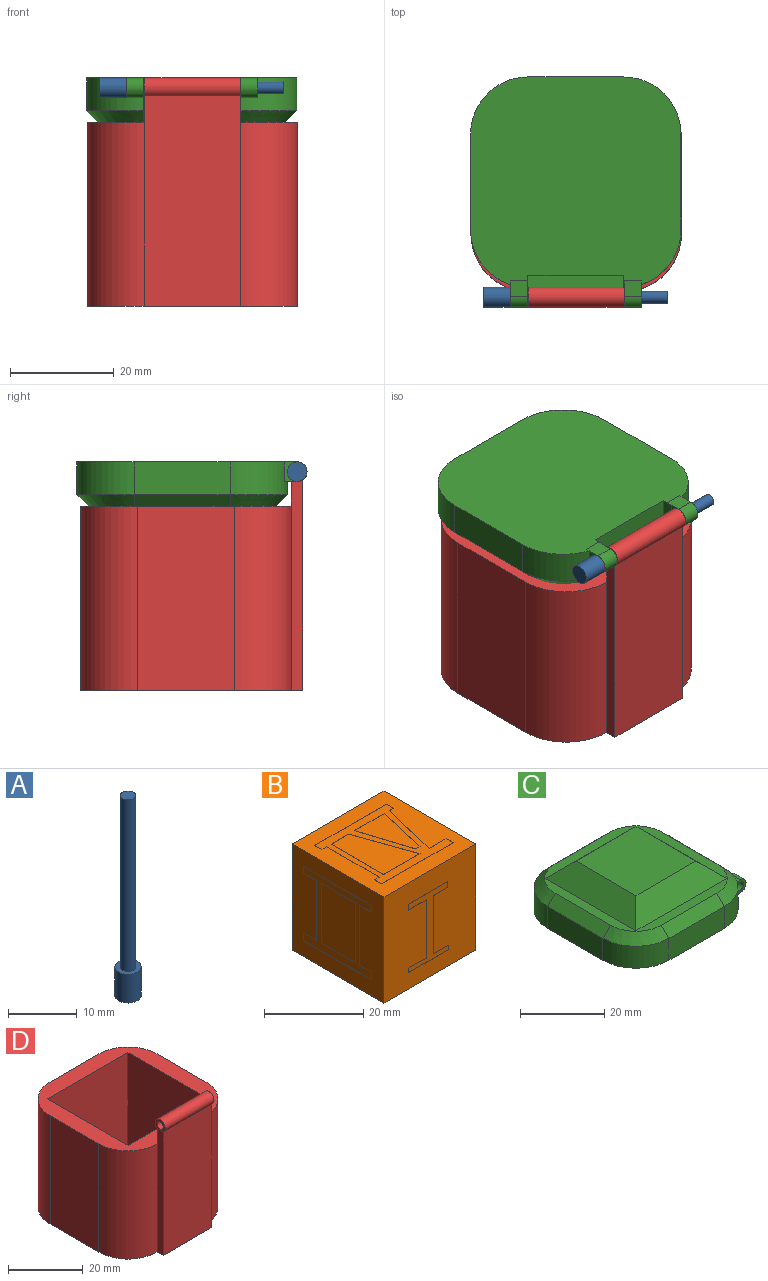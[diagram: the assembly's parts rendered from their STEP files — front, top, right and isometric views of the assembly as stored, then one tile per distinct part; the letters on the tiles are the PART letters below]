
ASSEMBLY  parts=4 mates=3
PART A: 5 faces, bbox 3.8x3.8x35.6 mm
  f0: cylinder r=1.91mm len=5.08mm, axis (0,0,-1), area 60.8mm2, adj f1,f2
  f1: plane 3.81x3.81mm, normal (0,0,1), area 7.4mm2, adj f0,f3
  f2: plane 3.81x3.81mm, normal (0,0,-1), area 11.4mm2, adj f0
  f3: cylinder r=1.13mm len=30.48mm, axis (0,0,-1), area 216.5mm2, adj f1,f4
  f4: plane 2.26x2.26mm, normal (0,0,1), area 4mm2, adj f3
PART B: 123 faces, bbox 26.2x26.2x26.2 mm
  f0: plane 26.16x26.16mm, normal (0,0,-1), area 443.9mm2, adj f1,f3,f4,f5,f106,f107,f108,f109
  f1: plane 26.16x26.16mm, normal (1,0,0), area 469.8mm2, adj f0,f2,f3,f5,f85,f86,f87,f88
  f2: plane 26.16x26.16mm, normal (0,0,1), area 361.8mm2, adj f1,f3,f4,f5,f62,f63,f64,f65
  f3: plane 26.16x26.16mm, normal (0,1,0), area 306.3mm2, adj f0,f1,f2,f4,f44,f45,f46,f47
  f4: plane 26.16x26.16mm, normal (-1,0,0), area 432mm2, adj f0,f2,f3,f5,f22,f23,f24,f25
  f5: plane 26.16x26.16mm, normal (0,-1,0), area 626mm2, adj f0,f1,f2,f4,f6,f7,f8,f9
  f6: plane 11.4x0.03mm, normal (0,0,1), area 0.3mm2, adj f5,f7,f17,f18
  f7: plane 1.1x0.03mm, normal (-1,0,0), area 0mm2, adj f5,f6,f8,f18
  f8: plane 4.28x0.03mm, normal (0,0,-1), area 0.1mm2, adj f5,f7,f9,f18
  f9: plane 14.35x0.03mm, normal (-1,0,0), area 0.4mm2, adj f5,f8,f10,f18
  f10: plane 4.1x0.03mm, normal (0,0,1), area 0.1mm2, adj f5,f9,f11,f18
  f11: plane 1.4x0.03mm, normal (-1,0,0), area 0mm2, adj f5,f10,f12,f18
  f12: plane 11.21x0.03mm, normal (0,0,-1), area 0.3mm2, adj f5,f11,f13,f18
  f13: plane 1.4x0.03mm, normal (1,0,0), area 0mm2, adj f5,f12,f14,f18
  f14: plane 5.01x0.03mm, normal (0,0,1), area 0.1mm2, adj f5,f13,f15,f18
  f15: plane 14.35x0.03mm, normal (1,0,0), area 0.4mm2, adj f5,f14,f16,f18
  f16: plane 5.01x0.03mm, normal (0,0,-1), area 0.1mm2, adj f5,f15,f17,f18
  f17: plane 1.1x0.03mm, normal (1,0,0), area 0mm2, adj f5,f6,f16,f18
  f18: plane 16.85x11.4mm, normal (0,-1,0), area 58.5mm2, adj f6,f7,f8,f9,f10,f11,f12,f13
  f19: plane 14.7x0.03mm, normal (0,1,0), area 0.4mm2, adj f20,f34,f35,f36
  f20: plane 9.66x0.03mm, normal (0,0,1), area 0.2mm2, adj f19,f21,f35,f36
  f21: plane 14.7x0.03mm, normal (0,-1,0), area 0.4mm2, adj f20,f34,f35,f36
  f22: plane 3.61x0.03mm, normal (0,0,1), area 0.1mm2, adj f4,f23,f33,f35
  f23: plane 14.7x0.03mm, normal (0,-1,0), area 0.4mm2, adj f4,f22,f24,f35
  f24: plane 3.61x0.03mm, normal (0,0,-1), area 0.1mm2, adj f4,f23,f25,f35
  f25: plane 1.97x0.03mm, normal (0,-1,0), area 0.1mm2, adj f4,f24,f26,f35
  f26: plane 19.19x0.03mm, normal (0,0,1), area 0.5mm2, adj f4,f25,f27,f35
  f27: plane 1.97x0.03mm, normal (0,1,0), area 0.1mm2, adj f4,f26,f28,f35
  f28: plane 3.2x0.03mm, normal (0,0,-1), area 0.1mm2, adj f4,f27,f29,f35
  f29: plane 14.7x0.03mm, normal (0,1,0), area 0.4mm2, adj f4,f28,f30,f35
  f30: plane 3.2x0.03mm, normal (0,0,1), area 0.1mm2, adj f4,f29,f31,f35
  f31: plane 1.7x0.03mm, normal (0,1,0), area 0mm2, adj f4,f30,f32,f35
  f32: plane 19.19x0.03mm, normal (0,0,-1), area 0.5mm2, adj f4,f31,f33,f35
  f33: plane 1.7x0.03mm, normal (0,-1,0), area 0mm2, adj f4,f22,f32,f35
  f34: plane 9.66x0.03mm, normal (0,0,-1), area 0.2mm2, adj f19,f21,f35,f36
  f35: plane 19.19x18.37mm, normal (-1,0,0), area 110.5mm2, adj f19,f20,f21,f22,f23,f24,f25,f26
  f36: plane 14.7x9.66mm, normal (-1,0,0), area 142mm2, adj f19,f20,f21,f34
  f37: plane 17.41x0.03mm, normal (1,0,0), area 0.4mm2, adj f38,f56,f57,f58
  f38: plane 10.84x0.03mm, normal (0,0,1), area 0.3mm2, adj f37,f39,f57,f58
  f39: plane 17.41x0.03mm, normal (-1,0,0), area 0.4mm2, adj f38,f40,f57,f58
  f40: plane 4.28x0.03mm, normal (0,0,-1), area 0.1mm2, adj f39,f41,f57,f58
  f41: plane 17.41x0.03mm, normal (1,0,0), area 0.4mm2, adj f40,f42,f57,f58
  f42: plane 2.29x0.03mm, normal (0,0,-1), area 0.1mm2, adj f41,f43,f57,f58
  f43: plane 17.41x0.03mm, normal (-1,0,0), area 0.4mm2, adj f42,f56,f57,f58
  f44: plane 3.21x0.03mm, normal (0,0,1), area 0.1mm2, adj f3,f45,f55,f57
  f45: plane 17.41x0.03mm, normal (-1,0,0), area 0.4mm2, adj f3,f44,f46,f57
  f46: plane 3.13x0.03mm, normal (0,0,-1), area 0.1mm2, adj f3,f45,f47,f57
  f47: plane 2.91x0.03mm, normal (-1,0,0), area 0.1mm2, adj f3,f46,f48,f57
  f48: plane 21x0.03mm, normal (0,0,1), area 0.5mm2, adj f3,f47,f49,f57
  f49: plane 2.91x0.03mm, normal (1,0,0), area 0.1mm2, adj f3,f48,f50,f57
  f50: plane 2.44x0.03mm, normal (0,0,-1), area 0.1mm2, adj f3,f49,f51,f57
  f51: plane 17.41x0.03mm, normal (1,0,0), area 0.4mm2, adj f3,f50,f52,f57
  f52: plane 2.6x0.03mm, normal (0,0,1), area 0.1mm2, adj f3,f51,f53,f57
  f53: plane 2.29x0.03mm, normal (1,0,0), area 0.1mm2, adj f3,f52,f54,f57
  f54: plane 21.23x0.03mm, normal (0,0,-1), area 0.5mm2, adj f3,f53,f55,f57
  f55: plane 2.29x0.03mm, normal (-1,0,0), area 0.1mm2, adj f3,f44,f54,f57
  f56: plane 4.28x0.03mm, normal (0,0,-1), area 0.1mm2, adj f37,f43,f57,f58
  f57: plane 22.6x21.23mm, normal (0,1,0), area 229.2mm2, adj f37,f38,f39,f40,f41,f42,f43,f44
  f58: plane 17.42x10.84mm, normal (0,1,0), area 149mm2, adj f37,f38,f39,f40,f41,f42,f43,f56
  f59: plane 13.23x4.2mm, normal (-0.95,-0.3,0), area 0.4mm2, adj f60,f78,f79,f81
  f60: plane 8.43x0.03mm, normal (0,1,0), area 0.2mm2, adj f59,f61,f79,f81
  f61: plane 13.23x3.04mm, normal (0.97,-0.22,0), area 0.3mm2, adj f60,f78,f79,f81
  f62: plane 15.01x0.03mm, normal (1,0,0), area 0.4mm2, adj f2,f63,f76,f79
  f63: plane 1.32x0.03mm, normal (0,-1,0), area 0mm2, adj f2,f62,f64,f79
  f64: plane 2.01x0.03mm, normal (1,0,0), area 0.1mm2, adj f2,f63,f65,f79
  f65: plane 20.35x0.03mm, normal (0,1,0), area 0.5mm2, adj f2,f64,f66,f79
  f66: plane 2.01x0.03mm, normal (-1,0,0), area 0.1mm2, adj f2,f65,f67,f79
  f67: plane 4.83x0.03mm, normal (0,-1,0), area 0.1mm2, adj f2,f66,f68,f79
  f68: plane 15.01x3.67mm, normal (-0.97,0.24,0), area 0.4mm2, adj f2,f67,f69,f79
  f69: plane 1.16x0.03mm, normal (0,1,0), area 0mm2, adj f2,f68,f70,f79
  f70: plane 2.01x0.03mm, normal (-1,0,0), area 0.1mm2, adj f2,f69,f71,f79
  f71: plane 20.35x0.03mm, normal (0,-1,0), area 0.5mm2, adj f2,f70,f72,f79
  f72: plane 2.01x0.03mm, normal (1,0,0), area 0.1mm2, adj f2,f71,f76,f79
  f73: plane 10.31x0.03mm, normal (0,-1,0), area 0.3mm2, adj f74,f77,f79,f80
  f74: plane 15.01x0.03mm, normal (-1,0,0), area 0.4mm2, adj f73,f75,f79,f80
  f75: plane 4.97x0.03mm, normal (0,1,0), area 0.1mm2, adj f74,f77,f79,f80
  f76: plane 1.32x0.03mm, normal (0,1,0), area 0mm2, adj f2,f62,f72,f79
  f77: plane 15.01x5.34mm, normal (0.94,0.34,0), area 0.4mm2, adj f73,f75,f79,f80
  f78: plane 1.19x0.03mm, normal (0,-1,0), area 0mm2, adj f59,f61,f79,f81
  f79: plane 20.35x19.03mm, normal (0,0,1), area 144.3mm2, adj f59,f60,f61,f62,f63,f64,f65,f66
  f80: plane 15.01x10.31mm, normal (0,0,1), area 114.7mm2, adj f73,f74,f75,f77
  f81: plane 13.23x8.43mm, normal (0,0,1), area 63.6mm2, adj f59,f60,f61,f78
  f82: plane 11.55x0.03mm, normal (0,0,1), area 0.3mm2, adj f83,f97,f98,f99
  f83: plane 14.24x4.47mm, normal (0,0.95,-0.3), area 0.4mm2, adj f82,f84,f98,f99
  f84: plane 3.03x0.03mm, normal (0,0,-1), area 0.1mm2, adj f83,f97,f98,f99
  f85: plane 17.06x0.03mm, normal (0,0,1), area 0.4mm2, adj f1,f86,f96,f98
  f86: plane 1.99x0.03mm, normal (0,-1,0), area 0.1mm2, adj f1,f85,f87,f98
  f87: plane 6.22x0.03mm, normal (0,0,-1), area 0.2mm2, adj f1,f86,f88,f98
  f88: plane 15.29x4.81mm, normal (0,-0.95,0.3), area 0.4mm2, adj f1,f87,f89,f98
  f89: plane 1.41x0.03mm, normal (0,0,1), area 0mm2, adj f1,f88,f90,f98
  f90: plane 1.99x0.03mm, normal (0,-1,0), area 0.1mm2, adj f1,f89,f91,f98
  f91: plane 17.06x0.03mm, normal (0,0,-1), area 0.4mm2, adj f1,f90,f92,f98
  f92: plane 1.99x0.03mm, normal (0,1,0), area 0.1mm2, adj f1,f91,f93,f98
  f93: plane 1.32x0.03mm, normal (0,0,1), area 0mm2, adj f1,f92,f94,f98
  f94: plane 15.29x4.67mm, normal (0,0.96,0.29), area 0.4mm2, adj f1,f93,f95,f98
  f95: plane 5.98x0.03mm, normal (0,0,-1), area 0.2mm2, adj f1,f94,f96,f98
  f96: plane 1.99x0.03mm, normal (0,1,0), area 0.1mm2, adj f1,f85,f95,f98
  f97: plane 14.24x4.04mm, normal (0,-0.96,-0.27), area 0.4mm2, adj f82,f84,f98,f99
  f98: plane 19.27x17.06mm, normal (1,0,0), area 110.9mm2, adj f82,f83,f84,f85,f86,f87,f88,f89
  f99: plane 14.24x11.55mm, normal (1,0,0), area 103.8mm2, adj f82,f83,f84,f97
  f100: plane 13.62x2.77mm, normal (-0.98,0.2,0), area 0.4mm2, adj f101,f119,f120,f122
  f101: plane 7.45x0.03mm, normal (0,-1,0), area 0.2mm2, adj f100,f102,f120,f122
  f102: plane 13.62x2.91mm, normal (0.98,0.21,0), area 0.4mm2, adj f101,f119,f120,f122
  f103: plane 14.8x0.03mm, normal (1,0,0), area 0.4mm2, adj f104,f117,f120,f121
  f104: plane 6.04x0.03mm, normal (0,1,0), area 0.2mm2, adj f103,f105,f120,f121
  f105: plane 14.8x3.41mm, normal (-0.97,-0.22,0), area 0.4mm2, adj f104,f117,f120,f121
  f106: plane 2.83x0.03mm, normal (0,1,0), area 0.1mm2, adj f0,f107,f118,f120
  f107: plane 14.8x0.03mm, normal (-1,0,0), area 0.4mm2, adj f0,f106,f108,f120
  f108: plane 2.83x0.03mm, normal (0,-1,0), area 0.1mm2, adj f0,f107,f109,f120
  f109: plane 1.44x0.03mm, normal (-1,0,0), area 0mm2, adj f0,f108,f110,f120
  f110: plane 18.56x0.03mm, normal (0,1,0), area 0.5mm2, adj f0,f109,f111,f120
  f111: plane 1.44x0.03mm, normal (1,0,0), area 0mm2, adj f0,f110,f112,f120
  f112: plane 1.34x0.03mm, normal (0,-1,0), area 0mm2, adj f0,f111,f113,f120
  f113: plane 14.8x3.5mm, normal (0.97,-0.23,0), area 0.4mm2, adj f0,f112,f114,f120
  f114: plane 4.83x0.03mm, normal (0,1,0), area 0.1mm2, adj f0,f113,f115,f120
  f115: plane 1.44x0.03mm, normal (1,0,0), area 0mm2, adj f0,f114,f116,f120
  f116: plane 18.56x0.03mm, normal (0,-1,0), area 0.5mm2, adj f0,f115,f118,f120
  f117: plane 2.63x0.03mm, normal (0,-1,0), area 0.1mm2, adj f103,f105,f120,f121
  f118: plane 1.44x0.03mm, normal (-1,0,0), area 0mm2, adj f0,f106,f116,f120
  f119: plane 1.77x0.03mm, normal (0,1,0), area 0mm2, adj f100,f102,f120,f122
  f120: plane 18.56x17.68mm, normal (0,0,-1), area 113.6mm2, adj f100,f101,f102,f103,f104,f105,f106,f107
  f121: plane 14.8x6.04mm, normal (0,0,-1), area 64.2mm2, adj f103,f104,f105,f117
  f122: plane 13.62x7.45mm, normal (0,0,-1), area 62.8mm2, adj f100,f101,f102,f119
PART C: 39 faces, bbox 44.5x40.7x14 mm
  f0: plane 3.35x3.09mm, normal (0,0,-1), area 10.4mm2, adj f1,f4,f5,f6
  f1: cylinder r=1.91mm len=3.81mm, axis (0,1,0), area 20.5mm2, adj f0,f3,f4,f5
  f2: cylinder r=1.14mm len=3.35mm, axis (0,1,0), area 24.1mm2, adj f4,f5
  f3: plane 3.36x2.36mm, normal (-0.01,0,1), area 6.7mm2, adj f1,f4,f5,f22
  f4: plane 4.36x3.81mm, normal (0,-1,0), area 10.9mm2, adj f0,f1,f2,f3,f22
  f5: plane 3.81x3.81mm, normal (0,1,0), area 8.8mm2, adj f0,f1,f2,f3,f22
  f6: plane 40.66x40.66mm, normal (0,0,-1), area 1497.3mm2, adj f0,f11,f13,f15,f16,f17,f20,f21
  f7: cylinder r=1.14mm len=3.35mm, axis (0,1,0), area 24.1mm2, adj f8,f12
  f8: plane 4.36x3.81mm, normal (0,1,0), area 10.9mm2, adj f7,f9,f10,f11,f13
  f9: plane 3.36x2.36mm, normal (-0.01,0,1), area 6.7mm2, adj f8,f10,f12,f13
  f10: cylinder r=1.91mm len=3.81mm, axis (0,1,0), area 20.5mm2, adj f8,f9,f11,f12
  f11: plane 3.35x3.09mm, normal (0,0,-1), area 10.4mm2, adj f6,f8,f10,f12
  f12: plane 3.81x3.81mm, normal (0,-1,0), area 8.8mm2, adj f7,f9,f10,f11,f13
  f13: cylinder r=11.05mm len=11.05mm, axis (0,0,-1), area 97.3mm2, adj f6,f8,f9,f12,f14,f15,f26,f31
  f14: plane 18.54x2.54mm, normal (1,0,0), area 47.1mm2, adj f13,f22,f24,f32
  f15: plane 18.54x6.35mm, normal (0,1,0), area 117.7mm2, adj f6,f13,f20,f28
  f16: plane 18.54x6.35mm, normal (-1,0,0), area 117.7mm2, adj f6,f20,f21,f29
  f17: plane 18.54x6.35mm, normal (0,-1,0), area 117.7mm2, adj f6,f21,f22,f25
  f18: plane 35.56x35.56mm, normal (0,0,1), area 288.8mm2, adj f23,f24,f25,f26,f27,f28,f29,f30
  f19: plane 20.07x20.07mm, normal (0,0,1), area 402.6mm2, adj f35,f36,f37,f38
  f20: cylinder r=11.05mm len=11.05mm, axis (0,0,1), area 110.2mm2, adj f6,f15,f16,f30
  f21: cylinder r=11.05mm len=11.05mm, axis (0,0,-1), area 110.2mm2, adj f6,f16,f17,f27
  f22: cylinder r=11.05mm len=11.05mm, axis (0,0,1), area 97.3mm2, adj f3,f4,f5,f6,f14,f17,f23,f33
  f23: cone r=8.51mm half-angle=45deg, axis (0,0,-1), area 55.2mm2, adj f18,f22,f24,f25
  f24: plane 18.54x2.54mm, normal (0.71,0,0.71), area 66.6mm2, adj f14,f18,f23,f26
  f25: plane 18.54x2.54mm, normal (0,-0.71,0.71), area 66.6mm2, adj f17,f18,f23,f27
  f26: cone r=8.51mm half-angle=45deg, axis (0,0,-1), area 55.2mm2, adj f13,f18,f24,f28
  f27: cone r=8.51mm half-angle=45deg, axis (0,0,-1), area 55.2mm2, adj f18,f21,f25,f29
  f28: plane 18.54x2.54mm, normal (0,0.71,0.71), area 66.6mm2, adj f15,f18,f26,f30
  f29: plane 18.54x2.54mm, normal (-0.71,0,0.71), area 66.6mm2, adj f16,f18,f27,f30
  f30: cone r=8.51mm half-angle=45deg, axis (0,0,-1), area 55.2mm2, adj f18,f20,f28,f29
  f31: plane 3.81x2.29mm, normal (0,-1,0), area 8.7mm2, adj f6,f13,f32,f34
  f32: plane 18.54x2.29mm, normal (0,0,-1), area 42.4mm2, adj f14,f31,f33,f34
  f33: plane 3.81x2.29mm, normal (0,1,0), area 8.7mm2, adj f6,f22,f32,f34
  f34: plane 18.54x3.81mm, normal (1,0,0), area 70.6mm2, adj f6,f31,f32,f33
  f35: plane 30.23x5.08mm, normal (0,-0.71,0.71), area 180.7mm2, adj f18,f19,f36,f37
  f36: plane 30.23x5.08mm, normal (0.71,0,0.71), area 180.7mm2, adj f18,f19,f35,f38
  f37: plane 30.23x5.08mm, normal (-0.71,0,0.71), area 180.7mm2, adj f18,f19,f35,f38
  f38: plane 30.23x5.08mm, normal (0,0.71,0.71), area 180.7mm2, adj f18,f19,f36,f37
PART D: 23 faces, bbox 40.6x43.7x44.1 mm
  f0: plane 40.64x40.64mm, normal (0,0,1), area 618mm2, adj f1,f2,f4,f5,f6,f7,f8,f10
  f1: plane 35.56x18.56mm, normal (1,0,0), area 660.2mm2, adj f0,f3,f11,f13
  f2: plane 35.56x18.56mm, normal (-1,0,0), area 660.2mm2, adj f0,f3,f10,f12
  f3: plane 42.93x40.64mm, normal (0,0,-1), area 1589.5mm2, adj f1,f2,f4,f10,f11,f12,f13,f15
  f4: plane 35.56x18.56mm, normal (0,1,0), area 660.2mm2, adj f0,f3,f10,f11
  f5: plane 31.5x30.48mm, normal (1,0,0), area 960mm2, adj f0,f6,f8,f9
  f6: plane 31.5x30.48mm, normal (0,1,0), area 960mm2, adj f0,f5,f7,f9
  f7: plane 31.5x30.48mm, normal (-1,0,0), area 960mm2, adj f0,f6,f8,f9
  f8: plane 31.5x30.48mm, normal (0,-1,0), area 960mm2, adj f0,f5,f7,f9
  f9: plane 30.48x30.48mm, normal (0,0,1), area 929mm2, adj f5,f6,f7,f8
  f10: cylinder r=11.04mm len=35.56mm, axis (0,0,-1), area 616.5mm2, adj f0,f2,f3,f4
  f11: cylinder r=11.04mm len=35.56mm, axis (0,0,1), area 616.5mm2, adj f0,f1,f3,f4
  f12: cylinder r=11.04mm len=35.56mm, axis (0,0,1), area 616.5mm2, adj f0,f2,f3,f15
  f13: cylinder r=11.04mm len=35.56mm, axis (0,0,-1), area 616.5mm2, adj f0,f1,f3,f16
  f14: plane 18.56x5.08mm, normal (0,1,0), area 94.3mm2, adj f0,f15,f16,f17
  f15: plane 40.64x2.29mm, normal (-1,0,0), area 92.9mm2, adj f3,f12,f14,f17,f18
  f16: plane 40.64x2.29mm, normal (1,0,0), area 92.9mm2, adj f3,f13,f14,f17,f18
  f17: plane 18.56x2.29mm, normal (0,0,1), area 1.2mm2, adj f14,f15,f16,f18,f20,f21,f22
  f18: plane 40.64x18.56mm, normal (0,-1,0), area 754.5mm2, adj f3,f15,f16,f17
  f19: cylinder r=1.15mm len=18.54mm, axis (-1,0,0), area 134.1mm2, adj f21,f22
  f20: cylinder r=1.91mm len=18.54mm, axis (-1,0,0), area 177.9mm2, adj f17,f21,f22
  f21: plane 3.81x3.45mm, normal (1,0,0), area 6.7mm2, adj f17,f19,f20
  f22: plane 3.81x3.45mm, normal (-1,0,0), area 6.7mm2, adj f17,f19,f20
PLACE A rot(axis=(0,1,0),90deg) t=(-13.8,-52.36,28.89)mm
PLACE B rot(axis=(-1,0,0),0deg) t=(4.56,-30.29,-9.23)mm
PLACE C rot(axis=(0.71,-0.71,0),180deg) t=(3.98,-30.14,26.99)mm
PLACE D rot(axis=(-1,0,0),0deg) t=(4.06,-10.56,4.49)mm
MATE revolute A.f0 <-> C.f1  axis (1,0,0) through (-8.72,-52.36,28.89)mm
MATE fastened C.f1 <-> D.f19  axis (-1,0,0) through (13.33,-52.36,28.89)mm
MATE fastened B.f122 <-> D.f9  axis (0,0,-1) through (4.06,-30.88,-9.23)mm
